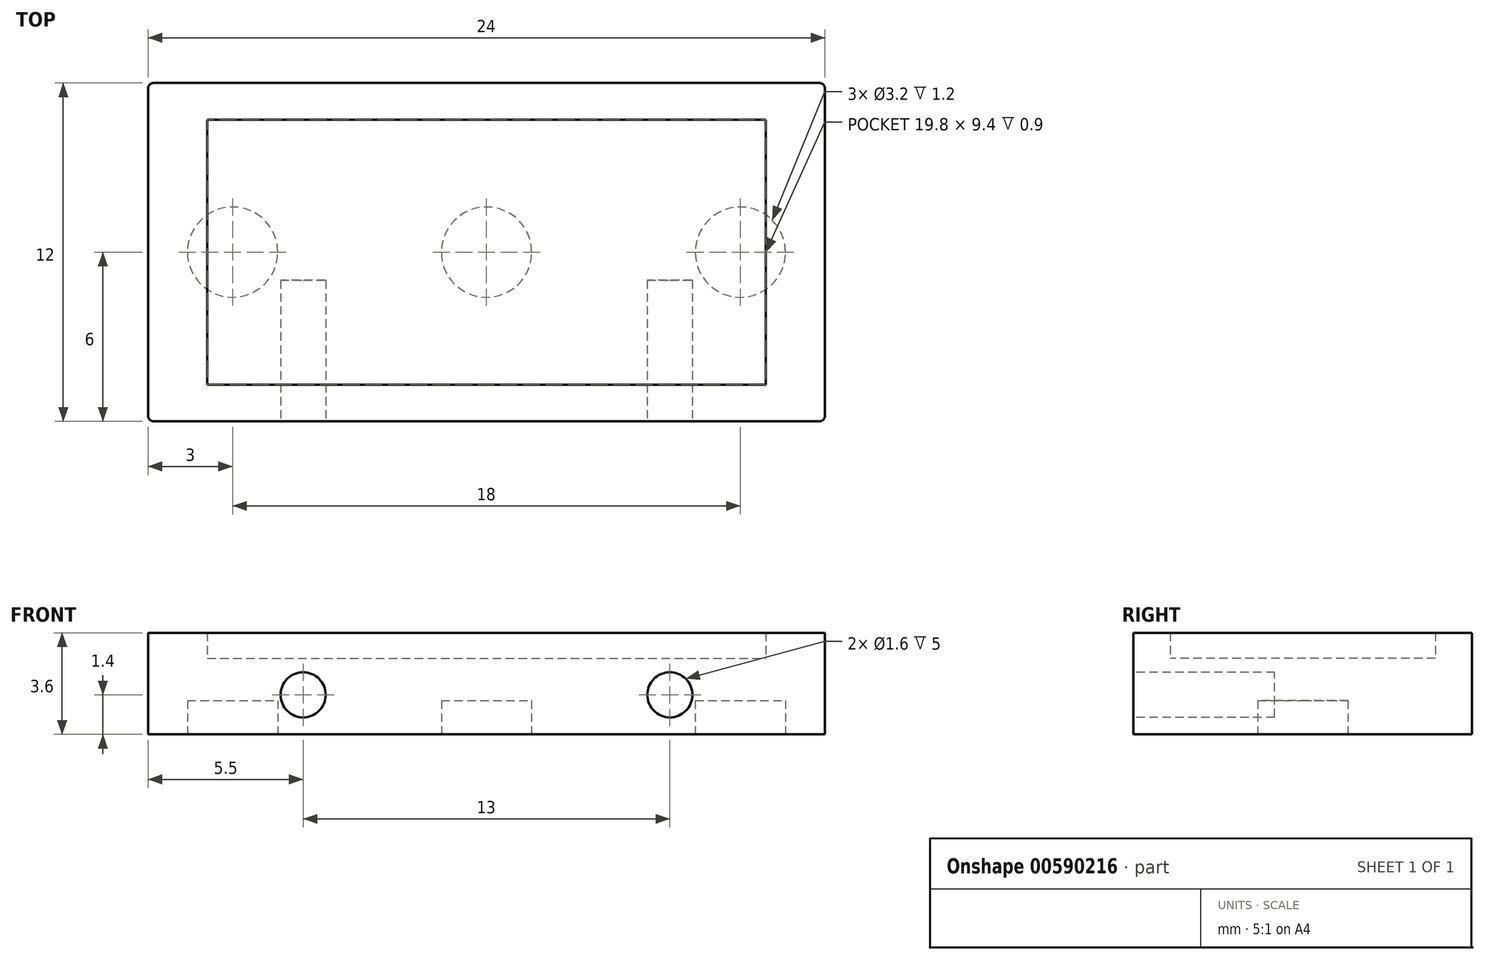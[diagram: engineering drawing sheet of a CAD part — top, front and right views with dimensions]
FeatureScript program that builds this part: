
annotation { "Feature Type Name" : "Feature", "Feature Type Description" : "" }
export const myFeature = defineFeature(function(context is Context, id is Id, definition is map)
    precondition{}
    {
        {
            var Q0;
            Q0=qCreatedBy(makeId("Top.planeOp"),FACE);
            var sketch = newSketch(context, id + "F0", { "sketchPlane" : qUnion([Q0])});
            skLineSegment(sketch, "E0.bottom", {"start": v(-12, 6) * mm, "end": v(12, 6) * mm});
            skLineSegment(sketch, "E0.top", {"start": v(-12, -6) * mm, "end": v(12, -6) * mm});
            skLineSegment(sketch, "E0.left", {"start": v(-12, 6) * mm, "end": v(-12, -6) * mm});
            skLineSegment(sketch, "E0.right", {"start": v(12, 6) * mm, "end": v(12, -6) * mm});
            skPoint(sketch, "E0.middle", {"position": v(0, 0) * mm});
            skLineSegment(sketch, "E1.bottom", {"start": v(-9.9, 4.7) * mm, "end": v(9.9, 4.7) * mm});
            skLineSegment(sketch, "E1.top", {"start": v(-9.9, -4.7) * mm, "end": v(9.9, -4.7) * mm});
            skLineSegment(sketch, "E1.left", {"start": v(-9.9, 4.7) * mm, "end": v(-9.9, -4.7) * mm});
            skLineSegment(sketch, "E1.right", {"start": v(9.9, 4.7) * mm, "end": v(9.9, -4.7) * mm});
            skSolve(sketch);
        }
        {
            var Q0;
            Q0=makeQuery(id+"F0.imprint","IMPRINT",FACE,{"disambiguationData":[TD([[makeQuery(id+"F0.imprint","IMPRINT",EDGE,{"derivedFrom":sQuery(id+"F0.wireOp",EDGE,"E0.bottom")}),-1.0]])]});
            extrude(context, id + "F1", {"entities" : qUnion([Q0]), "depth" : .9 * mm, "offsetDistance" : 25 * mm});
        }
        {
            var Q0;
            Q0=makeQuery(id+"F1.opExtrude","CAP_FACE",FACE,{"disambiguationData":[OSD([sQuery(id+"F0.wireOp",EDGE,"E0.bottom"),sQuery(id+"F0.wireOp",EDGE,"E0.top"),sQuery(id+"F0.wireOp",EDGE,"E0.left"),sQuery(id+"F0.wireOp",EDGE,"E0.right"),sQuery(id+"F0.wireOp",EDGE,"E1.bottom"),sQuery(id+"F0.wireOp",EDGE,"E1.top"),sQuery(id+"F0.wireOp",EDGE,"E1.left"),sQuery(id+"F0.wireOp",EDGE,"E1.right")])],"isStart":true});
            var sketch = newSketch(context, id + "F2", { "sketchPlane" : qUnion([Q0])});
            skLineSegment(sketch, "E2.bottom", {"start": v(12, 6) * mm, "end": v(-12, 6) * mm});
            skLineSegment(sketch, "E2.top", {"start": v(12, -6) * mm, "end": v(-12, -6) * mm});
            skLineSegment(sketch, "E2.left", {"start": v(12, 6) * mm, "end": v(12, -6) * mm});
            skLineSegment(sketch, "E2.right", {"start": v(-12, 6) * mm, "end": v(-12, -6) * mm});
            skPoint(sketch, "E2.middle", {"position": v(0, 0) * mm});
            skSolve(sketch);
        }
        {
            var Q0;
            Q0=qSketchRegion(id+"F2",true);
            extrude(context, id + "F3", {"entities" : qUnion([Q0]), "operationType" : NewBodyOperationType.ADD, "depth" : 2.7 * mm, "offsetDistance" : 25 * mm});
        }
        {
            var Q0;
            Q0=makeQuery(id+"F3.opExtrude","CAP_FACE",FACE,{"disambiguationData":[OSD([sQuery(id+"F2.wireOp",EDGE,"E2.bottom"),sQuery(id+"F2.wireOp",EDGE,"E2.top"),sQuery(id+"F2.wireOp",EDGE,"E2.left"),sQuery(id+"F2.wireOp",EDGE,"E2.right")])],"isStart":false});
            var sketch = newSketch(context, id + "F4", { "sketchPlane" : qUnion([Q0])});
            skCircle(sketch, "E3", {"center": v(0, 0) * mm, "radius": 1.6 * mm});
            skCircle(sketch, "E4", {"center": v(-9, 0) * mm, "radius": 1.6 * mm});
            skCircle(sketch, "E5", {"center": v(9, 0) * mm, "radius": 1.6 * mm});
            skSolve(sketch);
        }
        {
            var Q0;
            Q0=qSketchRegion(id+"F4",true);
            extrude(context, id + "F5", {"entities" : qUnion([Q0]), "operationType" : NewBodyOperationType.REMOVE, "oppositeDirection" : true, "depth" : 1.2 * mm, "offsetDistance" : 25 * mm});
        }
        {
            var Q0;
            Q0=makeQuery(id+"F3.boolean.opBoolean","MERGE",EDGE,{"derivedFrom":[makeQuery(id+"F1.opExtrude","SWEPT_EDGE",EDGE,{"disambiguationData":[OSD([sQuery(id+"F0.wireOp",EDGE,"jilFIhGa-1OLC-Nriz-qq6H-g09Lb7yk5Fd4.top"),sQuery(id+"F0.wireOp",EDGE,"jilFIhGa-1OLC-Nriz-qq6H-g09Lb7yk5Fd4.left")])]}),makeQuery(id+"F3.opExtrude","SWEPT_EDGE",EDGE,{"disambiguationData":[OSD([sQuery(id+"F2.wireOp",EDGE,"E2.bottom"),sQuery(id+"F2.wireOp",EDGE,"E2.right")])]})]});
            var Q1;
            Q1=makeQuery(id+"F3.boolean.opBoolean","MERGE",EDGE,{"derivedFrom":[makeQuery(id+"F1.opExtrude","SWEPT_EDGE",EDGE,{"disambiguationData":[OSD([sQuery(id+"F0.wireOp",EDGE,"jilFIhGa-1OLC-Nriz-qq6H-g09Lb7yk5Fd4.bottom"),sQuery(id+"F0.wireOp",EDGE,"jilFIhGa-1OLC-Nriz-qq6H-g09Lb7yk5Fd4.left")])]}),makeQuery(id+"F3.opExtrude","SWEPT_EDGE",EDGE,{"disambiguationData":[OSD([sQuery(id+"F2.wireOp",EDGE,"E2.top"),sQuery(id+"F2.wireOp",EDGE,"E2.right")])]})]});
            var Q2;
            Q2=makeQuery(id+"F3.boolean.opBoolean","MERGE",EDGE,{"derivedFrom":[makeQuery(id+"F1.opExtrude","SWEPT_EDGE",EDGE,{"disambiguationData":[OSD([sQuery(id+"F0.wireOp",EDGE,"jilFIhGa-1OLC-Nriz-qq6H-g09Lb7yk5Fd4.bottom"),sQuery(id+"F0.wireOp",EDGE,"jilFIhGa-1OLC-Nriz-qq6H-g09Lb7yk5Fd4.right")])]}),makeQuery(id+"F3.opExtrude","SWEPT_EDGE",EDGE,{"disambiguationData":[OSD([sQuery(id+"F2.wireOp",EDGE,"E2.top"),sQuery(id+"F2.wireOp",EDGE,"E2.left")])]})]});
            var Q3;
            Q3=makeQuery(id+"F3.boolean.opBoolean","MERGE",EDGE,{"derivedFrom":[makeQuery(id+"F1.opExtrude","SWEPT_EDGE",EDGE,{"disambiguationData":[OSD([sQuery(id+"F0.wireOp",EDGE,"jilFIhGa-1OLC-Nriz-qq6H-g09Lb7yk5Fd4.top"),sQuery(id+"F0.wireOp",EDGE,"jilFIhGa-1OLC-Nriz-qq6H-g09Lb7yk5Fd4.right")])]}),makeQuery(id+"F3.opExtrude","SWEPT_EDGE",EDGE,{"disambiguationData":[OSD([sQuery(id+"F2.wireOp",EDGE,"E2.bottom"),sQuery(id+"F2.wireOp",EDGE,"E2.left")])]})]});
            fillet(context, id + "F6", {"entities" : qUnion([Q0, Q1, Q2, Q3]), "radius" : .2 * mm, "tangentPropagation" : true, "allowEdgeOverflow" : false});
        }
        {
            var Q0;
            Q0=makeQuery(id+"F3.boolean.opBoolean","MERGE",FACE,{"derivedFrom":[makeQuery(id+"F1.opExtrude","SWEPT_FACE",FACE,{"disambiguationData":[OSD([sQuery(id+"F0.wireOp",EDGE,"jilFIhGa-1OLC-Nriz-qq6H-g09Lb7yk5Fd4.top")])]}),makeQuery(id+"F3.opExtrude","SWEPT_FACE",FACE,{"disambiguationData":[OSD([sQuery(id+"F2.wireOp",EDGE,"E2.bottom")])]})]});
            var sketch = newSketch(context, id + "F7", { "sketchPlane" : qUnion([Q0])});
            skCircle(sketch, "E6", {"center": v(-6.5, -1.3) * mm, "radius": 0.8 * mm});
            skCircle(sketch, "E7", {"center": v(6.5, -1.3) * mm, "radius": 0.8 * mm});
            skSolve(sketch);
        }
        {
            var Q0;
            Q0=qSketchRegion(id+"F7",true);
            extrude(context, id + "F8", {"entities" : qUnion([Q0]), "operationType" : NewBodyOperationType.REMOVE, "oppositeDirection" : true, "depth" : 5 * mm, "offsetDistance" : 25 * mm});
        }
    });
